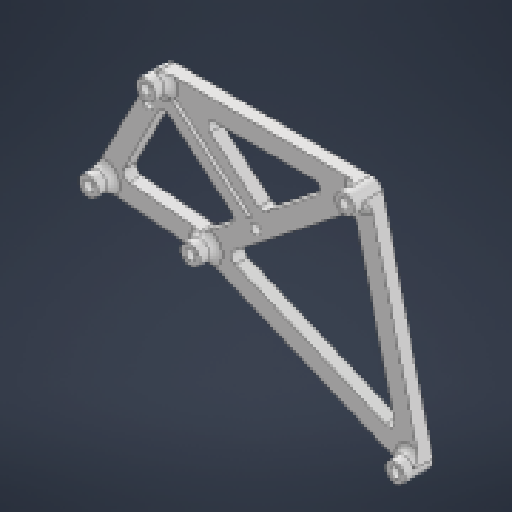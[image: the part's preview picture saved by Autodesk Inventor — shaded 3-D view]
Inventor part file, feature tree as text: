
AUTODESK INVENTOR PART (.ipt)
format: ipt  version: 2025 (Build 290162000, 162)  size: 419,840 bytes
history: native  units: mm
features: extrude x5, sketch x5, reference x5, fillet x2, other x2
ambient origin geometry x8: Origin, YZ Plane, XZ Plane, XY Plane, X Axis, Y Axis, Z Axis, Center Point
bodies: Solid1 (feature_tree)
feature tree (19):
  extrude  "Extrusion1"  Depth=6.0mm
  extrude  "Extrusion2"  Depth=6.0mm
  extrude  "Extrusion3"  Depth=6.0mm
  extrude  "Extrusion4"  Depth=6.0mm
  extrude  "Extrusion5"  Depth=2.0mm
  fillet  "Fillet2"  Radius=6.0mm
  fillet  "Fillet3"  Radius=4.0mm
  sketch  "Sketch1"  dims[d0=6.0mm d1=6.0mm]
  reference  "Reference1"
  reference  "Reference2"
  reference  "Reference3"
  reference  "Reference4"
  reference  "Reference5"
  sketch  "Sketch2"  dims[d2=6.0mm d3=6.0mm]
  sketch  "Sketch3"  dims[d4=6.0mm d5=6.0mm]
  sketch  "Sketch4"  dims[d6=6.0mm d7=6.0mm]
  sketch  "Sketch5"  dims[d8=6.0mm d9=6.0mm d10=6.0mm d11=4.0mm d12=0.0mm d18=10.0mm d19=0.0mm d21=0.05mm d22=0.05mm d23=0.05mm d24=0.05mm d25=0.05mm d26=4.0mm d27=0.0mm d28=3.1mm d29=3.1mm d30=3.1mm d31=3.1mm d32=3.1mm d36=6.981317mm d37=35.0mm d38=1.7mm d39=4.0mm d40=4.0mm d41=3.0mm d42=3.2mm d43=3.2mm d44=10.0mm d45=0.0mm d46=1.5mm d47=5.0mm d48=0.0mm d49=2.0mm d50=2.0mm]
  other  "Assembly1"
  other  "BTT E3 SKR MINI V3.0_3D:1"
